# Revit family: Pantalla Modelo LUX_LX650W
name_source: partatom
category: Luminarias
units: mm (PartAtom-declared; Revit-internal decimal feet)

## family parameters
Compartido = No
Corte con vacíos al cargar = No
Cota de conector redondo = Diámetro de uso
Origen de luz = No
Punto de cálculo de habitación = No
Se basa en plano de trabajo = Sí
Siempre vertical = No
Tipo de pieza = Normal

## types (3) — shared parameters
Comentarios de vataje = 90-260V
Espesor = 70 mm  [stored 0.229659 ft]
Fabricante = BRILLANT
Modulo alto = 343 mm
Modulo largo = 610 mm
Watt per fixture = 650
zero-valued in all types: Elevación por defecto

## per-type parameters (varying)
| type | Descripción | Lámpara | Modelo |
| Pantalla Modelo LUX_LX650W.2 | PANTALLA MODELO LUX, GABINETE LIGERO Y DELGADO, CODIGO LX650W.2, MODELO LUX 2, PIXEL PITCH 2.54MM, DENSIDAD FISICA LED 154,837 PIXEL/M2, TIPO DE LED SMD1514, CONFIGURACION DEL PIXEL 1R1G1B (3 EN 1), TAMAÑO DE GABINETE 609.92X343.08MM, RESOLUCION DE GABINETE 240X135 DOT, 2 PIEZAS POR CADA GABINETE/MODULO, PESO 10kg/PIEZA, MATERIAL DIE CAST ALUMINIO, BRILLO A 300-800 CD/M2, CONTRASTE >2000:1, ANGULO DE VISION 140 GRADOS EN HORIZONTAL Y EJE VERTICAL, ESCALA DE GRISES 14 BITS/8192 LEVEL, CONSUMO MAXIMO DE ENERGIA 650W, CONSUMO DE ENERGIA PROMEDIO 300W, DISTANCIA MINIMA DE VISUALIZACION 3M, FRECUENCIA DE ACTUALIZACION >2880Hz, TAMAÑO DEL MODULO 152.48X114.36MM, RESOLUCION 60X45, CORRIENTE CONSTANTE, TEMPERATURA DE OPERACIÓN -10 a 50C, AJUSTE DE BRILLO 0-100%, TEMPERATURA DE COLOR 5000K, 6500K, 9300K, 12000K, FUENTE DE ALIMENTACION AC90260V,50 60Hz, SEÑAL DE ENTRADA SVIDEO/RGB/RGBHV/YUV/YC, SISTEMA OPERATIVO WINDOWS (98, 2000, XP, VISTA), CONTROL POR SINCRONIZACION CON PC, DISTANCIA DE CONTROL UTP CAT5E:100M MULTI MODO, HUMEDAD DE FUNCIONAMIENTO 1090%RH, DURACION 10000Hrs, IP 43, PRECISION MONTAJE >1MM, TASA DE CONTROL 0.01%. | SMD 1514 | LX650W.2 |
| Pantalla Modelo LUX_LX650W.3 | PANTALLA MODELO LUX, GABINETE LIGERO Y DELGADO, CODIGO LX650W.3, MODELO LUX 3, PIXEL PITCH 1.58MM, DENSIDAD FISICA LED 396,384 PIXEL/M2, TIPO DE LED SMD1010, CONFIGURACION DEL PIXEL 1R1G1B (3 EN 1), TAMAÑO DE GABINETE 609.92X343.08MM, RESOLUCION DE GABINETE 384X216 DOT, 2 PIEZAS POR CADA GABINETE/MODULO, PESO 10kg/PIEZA, MATERIAL DIE CAST ALUMINIO, BRILLO A 300-800 CD/M2, CONTRASTE >2000:1, ANGULO DE VISION 140 GRADOS EN HORIZONTAL Y EJE VERTICAL, ESCALA DE GRISES 14 BITS/8192 LEVEL, CONSUMO MAXIMO DE ENERGIA 650W, CONSUMO DE ENERGIA PROMEDIO 300W, DISTANCIA MINIMA DE VISUALIZACION 2M, FRECUENCIA DE ACTUALIZACION >2880Hz, TAMAÑO DEL MODULO 152.48X114.36MM, RESOLUCION 96X72, CORRIENTE CONSTANTE, TEMPERATURA DE OPERACIÓN -10 a 50C, AJUSTE DE BRILLO 0-100%, TEMPERATURA DE COLOR 5000K, 6500K, 9300K, 12000K, FUENTE DE ALIMENTACION AC90260V,50 60Hz, SEÑAL DE ENTRADA SVIDEO/RGB/RGBHV/YUV/YC, SISTEMA OPERATIVO WINDOWS (98, 2000, XP, VISTA), CONTROL POR SINCRONIZACION CON PC, DISTANCIA DE CONTROL UTP CAT5E:100M MULTI MODO, HUMEDAD DE FUNCIONAMIENTO 1090%RH, DURACION 10000Hrs, IP 43, PRECISION MONTAJE >1MM, TASA DE CONTROL 0.01%.MODO, HUMEDAD DE FUNCIONAMIENTO 1090%RH, DURACION 10000Hrs, IP 43, PRECISION MONTAJE >1MM, TASA DE CONTROL 0.01%. | SMD 1010 | LX650W.3 |
| Pantalla Modelo LUX_LX650W.4 | PANTALLA MODELO LUX, GABINETE LIGERO Y DELGADO, CODIGO LX650W.4, MODELO LUX 4, PIXEL PITCH 1.9MM, DENSIDAD FISICA LED 275,267 PIXEL/M2, TIPO DE LED SMD1514, CONFIGURACION DEL PIXEL 1R1G1B (3 EN 1), TAMAÑO DE GABINETE 609.92X343.08MM, RESOLUCION DE GABINETE 384X216 DOT, 2 PIEZAS POR CADA GABINETE/MODULO, PESO 10kg/PIEZA, MATERIAL DIE CAST ALUMINIO, BRILLO A 300-800 CD/M2, CONTRASTE >2000:1, ANGULO DE VISION 140 GRADOS EN HORIZONTAL Y EJE VERTICAL, ESCALA DE GRISES 14 BITS/8192 LEVEL, CONSUMO MAXIMO DE ENERGIA 650W, CONSUMO DE ENERGIA PROMEDIO 300W, DISTANCIA MINIMA DE VISUALIZACION 2M, FRECUENCIA DE ACTUALIZACION >2880Hz, TAMAÑO DEL MODULO 152.48X114.36MM, RESOLUCION 80X60, CORRIENTE CONSTANTE, TEMPERATURA DE OPERACIÓN -10 a 50C, AJUSTE DE BRILLO 0-100%, TEMPERATURA DE COLOR 5000K, 6500K, 9300K, 12000K, FUENTE DE ALIMENTACION AC90260V,50 60Hz, SEÑAL DE ENTRADA SVIDEO/RGB/RGBHV/YUV/YC, SISTEMA OPERATIVO WINDOWS (98, 2000, XP, VISTA), CONTROL POR SINCRONIZACION CON PC, DISTANCIA DE CONTROL UTP CAT5E:100M MULTI MODO, HUMEDAD DE FUNCIONAMIENTO 1090%RH, DURACION 10000Hrs, IP 43, PRECISION MONTAJE >1MM, TASA DE CONTROL 0.01%. | SMD 1514 | LX650W.4 |

note: [stored X ft] marks values corroborated as IEEE doubles in the binary element streams (Revit-internal decimal feet)

## geometry (parser evidence)
native form markers: Blend x2
no freeform markers — native parametric forms only
